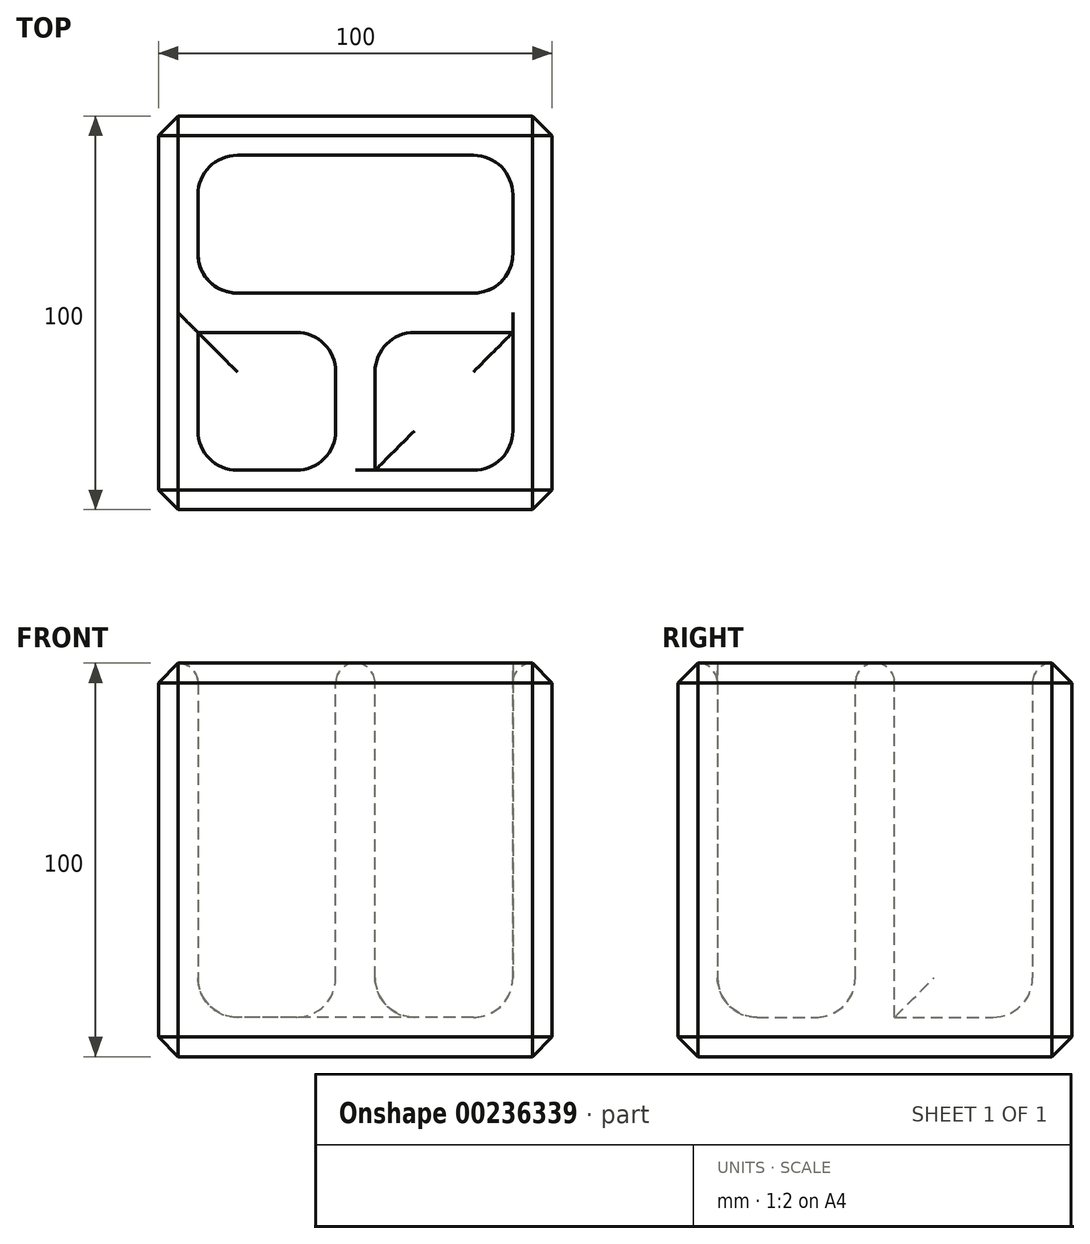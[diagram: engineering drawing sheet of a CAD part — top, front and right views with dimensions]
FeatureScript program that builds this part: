
annotation { "Feature Type Name" : "Feature", "Feature Type Description" : "" }
export const myFeature = defineFeature(function(context is Context, id is Id, definition is map)
    precondition{}
    {
        {
            var Q0;
            Q0=qCreatedBy(makeId("Top.planeOp"),FACE);
            var sketch = newSketch(context, id + "F0", { "sketchPlane" : qUnion([Q0])});
            skLineSegment(sketch, "E0.bottom", {"start": v(50, -50) * mm, "end": v(-50, -50) * mm});
            skLineSegment(sketch, "E0.top", {"start": v(50, 50) * mm, "end": v(-50, 50) * mm});
            skLineSegment(sketch, "E0.left", {"start": v(50, -50) * mm, "end": v(50, 50) * mm});
            skLineSegment(sketch, "E0.right", {"start": v(-50, -50) * mm, "end": v(-50, 50) * mm});
            skPoint(sketch, "E0.middle", {"position": v(0, 0) * mm});
            skSolve(sketch);
        }
        {
            var Q0;
            Q0 = qSketchRegion(id + "F0", true);
            extrude(context, id + "F1", {"entities" : qUnion([Q0]), "depth" : 100 * mm});
        }
        {
            var Q0;
            Q0=makeQuery(id+"F1.opExtrude","CAP_FACE",FACE,{"disambiguationData":[OSD([sQuery(id+"F0.wireOp",EDGE,"E0.bottom"),sQuery(id+"F0.wireOp",EDGE,"E0.top"),sQuery(id+"F0.wireOp",EDGE,"E0.left"),sQuery(id+"F0.wireOp",EDGE,"E0.right")])],"isStart":false});
            shell(context, id + "F2", {"entities" : qUnion([Q0]), "thickness" : 10 * mm});
        }
        {
            var Q0;
            Q0=makeQuery(id+"F1.opExtrude","CAP_FACE",FACE,{"disambiguationData":[OSD([sQuery(id+"F0.wireOp",EDGE,"E0.bottom"),sQuery(id+"F0.wireOp",EDGE,"E0.top"),sQuery(id+"F0.wireOp",EDGE,"E0.left"),sQuery(id+"F0.wireOp",EDGE,"E0.right")])],"isStart":false});
            var sketch = newSketch(context, id + "F3", { "sketchPlane" : qUnion([Q0])});
            skLineSegment(sketch, "E1", {"start": v(-40, -40) * mm, "end": v(-40, -5) * mm});
            skLineSegment(sketch, "E2", {"start": v(-40, 40) * mm, "end": v(-40, 5) * mm});
            skLineSegment(sketch, "E3", {"start": v(-40, -5) * mm, "end": v(-40, 5) * mm});
            skLineSegment(sketch, "E4", {"start": v(-40, -5) * mm, "end": v(40, -5) * mm});
            skLineSegment(sketch, "E5", {"start": v(-40, 5) * mm, "end": v(40, 5) * mm});
            skLineSegment(sketch, "E6", {"start": v(-40, 5) * mm, "end": v(-5, 5) * mm});
            skLineSegment(sketch, "E7", {"start": v(-5, 5) * mm, "end": v(5, 5) * mm});
            skLineSegment(sketch, "E8", {"start": v(-5, 5) * mm, "end": v(-5, 40) * mm});
            skLineSegment(sketch, "E9", {"start": v(-5, 5) * mm, "end": v(-5, -5) * mm});
            skLineSegment(sketch, "E10", {"start": v(-5, -5) * mm, "end": v(-5, -40) * mm});
            skLineSegment(sketch, "E11", {"start": v(5, 5) * mm, "end": v(5, 40) * mm});
            skLineSegment(sketch, "E12", {"start": v(5, 5) * mm, "end": v(5, -40) * mm});
            skSolve(sketch);
        }
        {
            var Q0;
            Q0 = qSketchRegion(id + "F3", true);
            var Q1;
            {var subQ0=sQuery(id+"F3.wireOp",EDGE,"E10");Q1=makeQuery(id+"F3.imprint","IMPRINT",FACE,{"disambiguationData":[TD([[makeQuery(id+"F3.imprint","IMPRINT",EDGE,{"derivedFrom":subQ0}),1.0]])]});}
            var Q2;
            Q2=makeQuery(id+"F3.imprint","IMPRINT",FACE,{"disambiguationData":[TD([[makeQuery(id+"F3.imprint","IMPRINT",EDGE,{"derivedFrom":sQuery(id+"F3.wireOp",EDGE,"E7")}),1.0]])]});
            var Q3;
            {var subQ6=sQuery(id+"F3.wireOp",EDGE,"E5");Q3=makeQuery(id+"F3.imprint","IMPRINT",FACE,{"disambiguationData":[TD([[makeQuery(id+"F3.imprint","IMPRINT",EDGE,{"derivedFrom":subQ6}),-1.0]])]});}
            extrude(context, id + "F4", {"entities" : qUnion([Q0, Q1, Q2, Q3]), "operationType" : NewBodyOperationType.ADD, "endBound" : BoundingType.UP_TO_NEXT, "oppositeDirection" : true, "depth" : 25 * mm});
        }
        {
            var Q0;
            Q0=makeQuery(id+"F1.opExtrude","CAP_EDGE",EDGE,{"disambiguationData":[OSD([sQuery(id+"F0.wireOp",EDGE,"E0.left")])],"isStart":false});
            var Q1;
            Q1=makeQuery(id+"F1.opExtrude","CAP_EDGE",EDGE,{"disambiguationData":[OSD([sQuery(id+"F0.wireOp",EDGE,"E0.bottom")])],"isStart":false});
            var Q2;
            Q2=makeQuery(id+"F1.opExtrude","CAP_EDGE",EDGE,{"disambiguationData":[OSD([sQuery(id+"F0.wireOp",EDGE,"E0.top")])],"isStart":false});
            var Q3;
            Q3=makeQuery(id+"F1.opExtrude","CAP_EDGE",EDGE,{"disambiguationData":[OSD([sQuery(id+"F0.wireOp",EDGE,"E0.right")])],"isStart":false});
            var Q4;
            Q4=makeQuery(id+"F1.opExtrude","SWEPT_EDGE",EDGE,{"disambiguationData":[OSD([sQuery(id+"F0.wireOp",EDGE,"E0.bottom"),sQuery(id+"F0.wireOp",EDGE,"E0.left")])]});
            var Q5;
            Q5=makeQuery(id+"F1.opExtrude","CAP_EDGE",EDGE,{"disambiguationData":[OSD([sQuery(id+"F0.wireOp",EDGE,"E0.left")])],"isStart":true});
            var Q6;
            Q6=makeQuery(id+"F1.opExtrude","CAP_EDGE",EDGE,{"disambiguationData":[OSD([sQuery(id+"F0.wireOp",EDGE,"E0.bottom")])],"isStart":true});
            var Q7;
            Q7=makeQuery(id+"F1.opExtrude","SWEPT_EDGE",EDGE,{"disambiguationData":[OSD([sQuery(id+"F0.wireOp",EDGE,"E0.bottom"),sQuery(id+"F0.wireOp",EDGE,"E0.right")])]});
            var Q8;
            Q8=makeQuery(id+"F1.opExtrude","CAP_EDGE",EDGE,{"disambiguationData":[OSD([sQuery(id+"F0.wireOp",EDGE,"E0.right")])],"isStart":true});
            var Q9;
            Q9=makeQuery(id+"F1.opExtrude","SWEPT_EDGE",EDGE,{"disambiguationData":[OSD([sQuery(id+"F0.wireOp",EDGE,"E0.top"),sQuery(id+"F0.wireOp",EDGE,"E0.right")])]});
            var Q10;
            Q10=makeQuery(id+"F1.opExtrude","CAP_EDGE",EDGE,{"disambiguationData":[OSD([sQuery(id+"F0.wireOp",EDGE,"E0.top")])],"isStart":true});
            var Q11;
            Q11=makeQuery(id+"F1.opExtrude","SWEPT_EDGE",EDGE,{"disambiguationData":[OSD([sQuery(id+"F0.wireOp",EDGE,"E0.top"),sQuery(id+"F0.wireOp",EDGE,"E0.left")])]});
            chamfer(context, id + "F5", {"entities" : qUnion([Q0, Q1, Q2, Q3, Q4, Q5, Q6, Q7, Q8, Q9, Q10, Q11]), "width" : 5 * mm, "tangentPropagation" : true});
        }
        {
            var Q0;
            Q0=makeQuery(id+"F2.opShell","OFFSET_EDGE",EDGE,{"disambiguationData":[OSD([sQuery(id+"F0.wireOp",EDGE,"E0.bottom"),sQuery(id+"F0.wireOp",EDGE,"E0.right")])]});
            var Q1;
            {var subQ0=sQuery(id+"F0.wireOp",EDGE,"E0.bottom");var subQ1=sQuery(id+"F0.wireOp",EDGE,"E0.right");Q1=makeQuery(id+"F4.boolean.opBoolean","SPLIT",EDGE,{"disambiguationData":[TD([makeQuery(id+"F2.opShell","OFFSET_FACE",FACE,{"disambiguationData":[OSD([subQ0])]})])],"derivedFrom":makeQuery(id+"F2.opShell","OFFSET_EDGE",EDGE,{"disambiguationData":[OSD([subQ1]),TDD([makeQuery(id+"F1.opExtrude","CAP_EDGE",EDGE,{"disambiguationData":[OSD([subQ1])],"isStart":true})])]})});}
            var Q2;
            Q2=makeQuery(id+"F4.opExtrude","SWEPT_EDGE",EDGE,{"disambiguationData":[OSD([sQuery(id+"F3.wireOp",EDGE,"E1"),sQuery(id+"F3.wireOp",EDGE,"E3"),sQuery(id+"F3.wireOp",EDGE,"E4")])]});
            var Q3;
            {var subQ0=sQuery(id+"F3.wireOp",EDGE,"E4");Q3=makeQuery(id+"F4.opExtrude","CAP_EDGE",EDGE,{"disambiguationData":[OSD([subQ0]),TDD([makeQuery(id+"F3.imprint","IMPRINT",EDGE,{"disambiguationData":[TD([[makeQuery(id+"F3.imprint","INTERSECT",VERTEX,{"derivedFrom":[sQuery(id+"F3.wireOp",EDGE,"E1"),sQuery(id+"F3.wireOp",EDGE,"E3"),subQ0]}),-1.0]])],"derivedFrom":subQ0})])],"isStart":false});}
            var Q4;
            Q4=makeQuery(id+"F4.opExtrude","CAP_EDGE",EDGE,{"disambiguationData":[OSD([sQuery(id+"F3.wireOp",EDGE,"E10")])],"isStart":false});
            var Q5;
            {var subQ0=sQuery(id+"F0.wireOp",EDGE,"E0.bottom");var subQ1=sQuery(id+"F0.wireOp",EDGE,"E0.right");Q5=makeQuery(id+"F4.boolean.opBoolean","SPLIT",EDGE,{"disambiguationData":[TD([makeQuery(id+"F2.opShell","OFFSET_FACE",FACE,{"disambiguationData":[OSD([subQ1])]})])],"derivedFrom":makeQuery(id+"F2.opShell","OFFSET_EDGE",EDGE,{"disambiguationData":[OSD([subQ0]),TDD([makeQuery(id+"F1.opExtrude","CAP_EDGE",EDGE,{"disambiguationData":[OSD([subQ0])],"isStart":true})])]})});}
            var Q6;
            Q6=makeQuery(id+"F4.opExtrude","SWEPT_EDGE",EDGE,{"disambiguationData":[OSD([sQuery(id+"F3.wireOp",EDGE,"E4"),sQuery(id+"F3.wireOp",EDGE,"E9"),sQuery(id+"F3.wireOp",EDGE,"E10")])]});
            var Q7;
            Q7=makeQuery(id+"F4.opExtrude","SWEPT_EDGE",EDGE,{"disambiguationData":[OSD([sQuery(id+"F0.wireOp",EDGE,"E0.bottom"),sQuery(id+"F3.wireOp",EDGE,"E10")])]});
            var Q8;
            Q8=makeQuery(id+"F4.opExtrude","SWEPT_EDGE",EDGE,{"disambiguationData":[OSD([sQuery(id+"F3.wireOp",EDGE,"E2"),sQuery(id+"F3.wireOp",EDGE,"E3"),sQuery(id+"F3.wireOp",EDGE,"E6")])]});
            var Q9;
            {var subQ0=sQuery(id+"F0.wireOp",EDGE,"E0.right");var subQ1=sQuery(id+"F0.wireOp",EDGE,"E0.top");Q9=makeQuery(id+"F4.boolean.opBoolean","SPLIT",EDGE,{"disambiguationData":[TD([makeQuery(id+"F2.opShell","OFFSET_FACE",FACE,{"disambiguationData":[OSD([subQ1])]})])],"derivedFrom":makeQuery(id+"F2.opShell","OFFSET_EDGE",EDGE,{"disambiguationData":[OSD([subQ0]),TDD([makeQuery(id+"F1.opExtrude","CAP_EDGE",EDGE,{"disambiguationData":[OSD([subQ0])],"isStart":true})])]})});}
            var Q10;
            Q10=makeQuery(id+"F4.opExtrude","CAP_EDGE",EDGE,{"disambiguationData":[OSD([sQuery(id+"F3.wireOp",EDGE,"E6")])],"isStart":false});
            var Q11;
            Q11=makeQuery(id+"F2.opShell","OFFSET_EDGE",EDGE,{"disambiguationData":[OSD([sQuery(id+"F0.wireOp",EDGE,"E0.top"),sQuery(id+"F0.wireOp",EDGE,"E0.right")])]});
            var Q12;
            {var subQ0=sQuery(id+"F0.wireOp",EDGE,"E0.right");var subQ1=sQuery(id+"F0.wireOp",EDGE,"E0.top");Q12=makeQuery(id+"F4.boolean.opBoolean","SPLIT",EDGE,{"disambiguationData":[TD([makeQuery(id+"F2.opShell","OFFSET_FACE",FACE,{"disambiguationData":[OSD([subQ0])]})])],"derivedFrom":makeQuery(id+"F2.opShell","OFFSET_EDGE",EDGE,{"disambiguationData":[OSD([subQ1]),TDD([makeQuery(id+"F1.opExtrude","CAP_EDGE",EDGE,{"disambiguationData":[OSD([subQ1])],"isStart":true})])]})});}
            var Q13;
            Q13=makeQuery(id+"F4.opExtrude","CAP_EDGE",EDGE,{"disambiguationData":[OSD([sQuery(id+"F3.wireOp",EDGE,"E8")])],"isStart":false});
            var Q14;
            Q14=makeQuery(id+"F4.opExtrude","SWEPT_EDGE",EDGE,{"disambiguationData":[OSD([sQuery(id+"F3.wireOp",EDGE,"E6"),sQuery(id+"F3.wireOp",EDGE,"E7"),sQuery(id+"F3.wireOp",EDGE,"E8"),sQuery(id+"F3.wireOp",EDGE,"E9")])]});
            var Q15;
            Q15=makeQuery(id+"F4.opExtrude","SWEPT_EDGE",EDGE,{"disambiguationData":[OSD([sQuery(id+"F0.wireOp",EDGE,"E0.top"),sQuery(id+"F3.wireOp",EDGE,"E8")])]});
            var Q16;
            Q16=makeQuery(id+"F4.opExtrude","CAP_EDGE",EDGE,{"disambiguationData":[OSD([sQuery(id+"F3.wireOp",EDGE,"E12")])],"isStart":false});
            var Q17;
            Q17=makeQuery(id+"F4.opExtrude","CAP_EDGE",EDGE,{"disambiguationData":[OSD([sQuery(id+"F3.wireOp",EDGE,"E11")])],"isStart":false});
            var Q18;
            {var subQ0=sQuery(id+"F0.wireOp",EDGE,"E0.left");var subQ1=sQuery(id+"F0.wireOp",EDGE,"E0.top");Q18=makeQuery(id+"F4.boolean.opBoolean","SPLIT",EDGE,{"disambiguationData":[TD([makeQuery(id+"F2.opShell","OFFSET_FACE",FACE,{"disambiguationData":[OSD([subQ0])]})])],"derivedFrom":makeQuery(id+"F2.opShell","OFFSET_EDGE",EDGE,{"disambiguationData":[OSD([subQ1]),TDD([makeQuery(id+"F1.opExtrude","CAP_EDGE",EDGE,{"disambiguationData":[OSD([subQ1])],"isStart":true})])]})});}
            var Q19;
            Q19=makeQuery(id+"F4.opExtrude","SWEPT_EDGE",EDGE,{"disambiguationData":[OSD([sQuery(id+"F0.wireOp",EDGE,"E0.top"),sQuery(id+"F3.wireOp",EDGE,"E11")])]});
            var Q20;
            Q20=makeQuery(id+"F4.opExtrude","SWEPT_EDGE",EDGE,{"disambiguationData":[OSD([sQuery(id+"F3.wireOp",EDGE,"E5"),sQuery(id+"F3.wireOp",EDGE,"E7"),sQuery(id+"F3.wireOp",EDGE,"E11"),sQuery(id+"F3.wireOp",EDGE,"E12")])]});
            var Q21;
            Q21=makeQuery(id+"F4.opExtrude","CAP_EDGE",EDGE,{"disambiguationData":[OSD([sQuery(id+"F3.wireOp",EDGE,"E5")])],"isStart":false});
            var Q22;
            Q22=makeQuery(id+"F2.opShell","OFFSET_EDGE",EDGE,{"disambiguationData":[OSD([sQuery(id+"F0.wireOp",EDGE,"E0.top"),sQuery(id+"F0.wireOp",EDGE,"E0.left")])]});
            var Q23;
            {var subQ0=sQuery(id+"F0.wireOp",EDGE,"E0.left");var subQ1=sQuery(id+"F0.wireOp",EDGE,"E0.top");Q23=makeQuery(id+"F4.boolean.opBoolean","SPLIT",EDGE,{"disambiguationData":[TD([makeQuery(id+"F2.opShell","OFFSET_FACE",FACE,{"disambiguationData":[OSD([subQ1])]})])],"derivedFrom":makeQuery(id+"F2.opShell","OFFSET_EDGE",EDGE,{"disambiguationData":[OSD([subQ0]),TDD([makeQuery(id+"F1.opExtrude","CAP_EDGE",EDGE,{"disambiguationData":[OSD([subQ0])],"isStart":true})])]})});}
            var Q24;
            Q24=makeQuery(id+"F4.opExtrude","SWEPT_EDGE",EDGE,{"disambiguationData":[OSD([sQuery(id+"F0.wireOp",EDGE,"E0.left"),sQuery(id+"F3.wireOp",EDGE,"E5")])]});
            var Q25;
            Q25=makeQuery(id+"F4.opExtrude","SWEPT_EDGE",EDGE,{"disambiguationData":[OSD([sQuery(id+"F3.wireOp",EDGE,"E4"),sQuery(id+"F3.wireOp",EDGE,"E12")])]});
            var Q26;
            {var subQ0=sQuery(id+"F3.wireOp",EDGE,"E4");Q26=makeQuery(id+"F4.opExtrude","CAP_EDGE",EDGE,{"disambiguationData":[OSD([subQ0]),TDD([makeQuery(id+"F3.imprint","IMPRINT",EDGE,{"disambiguationData":[TD([[makeQuery(id+"F3.imprint","INTERSECT",VERTEX,{"derivedFrom":[subQ0,sQuery(id+"F3.wireOp",EDGE,"E12")]}),-1.0]])],"derivedFrom":subQ0})])],"isStart":false});}
            var Q27;
            Q27=makeQuery(id+"F4.opExtrude","SWEPT_EDGE",EDGE,{"disambiguationData":[OSD([sQuery(id+"F0.wireOp",EDGE,"E0.bottom"),sQuery(id+"F3.wireOp",EDGE,"E12")])]});
            var Q28;
            {var subQ0=sQuery(id+"F0.wireOp",EDGE,"E0.bottom");var subQ1=sQuery(id+"F0.wireOp",EDGE,"E0.left");Q28=makeQuery(id+"F4.boolean.opBoolean","SPLIT",EDGE,{"disambiguationData":[TD([makeQuery(id+"F2.opShell","OFFSET_FACE",FACE,{"disambiguationData":[OSD([subQ1])]})])],"derivedFrom":makeQuery(id+"F2.opShell","OFFSET_EDGE",EDGE,{"disambiguationData":[OSD([subQ0]),TDD([makeQuery(id+"F1.opExtrude","CAP_EDGE",EDGE,{"disambiguationData":[OSD([subQ0])],"isStart":true})])]})});}
            var Q29;
            {var subQ0=sQuery(id+"F0.wireOp",EDGE,"E0.bottom");var subQ1=sQuery(id+"F0.wireOp",EDGE,"E0.left");Q29=makeQuery(id+"F4.boolean.opBoolean","SPLIT",EDGE,{"disambiguationData":[TD([makeQuery(id+"F2.opShell","OFFSET_FACE",FACE,{"disambiguationData":[OSD([subQ0])]})])],"derivedFrom":makeQuery(id+"F2.opShell","OFFSET_EDGE",EDGE,{"disambiguationData":[OSD([subQ1]),TDD([makeQuery(id+"F1.opExtrude","CAP_EDGE",EDGE,{"disambiguationData":[OSD([subQ1])],"isStart":true})])]})});}
            var Q30;
            Q30=makeQuery(id+"F4.opExtrude","SWEPT_EDGE",EDGE,{"disambiguationData":[OSD([sQuery(id+"F0.wireOp",EDGE,"E0.left"),sQuery(id+"F3.wireOp",EDGE,"E4")])]});
            var Q31;
            Q31=makeQuery(id+"F2.opShell","OFFSET_EDGE",EDGE,{"disambiguationData":[OSD([sQuery(id+"F0.wireOp",EDGE,"E0.bottom"),sQuery(id+"F0.wireOp",EDGE,"E0.left")])]});
            fillet(context, id + "F6", {"entities" : qUnion([Q0, Q1, Q2, Q3, Q4, Q5, Q6, Q7, Q8, Q9, Q10, Q11, Q12, Q13, Q14, Q15, Q16, Q17, Q18, Q19, Q20, Q21, Q22, Q23, Q24, Q25, Q26, Q27, Q28, Q29, Q30, Q31]), "radius" : 10 * mm, "tangentPropagation" : true, "allowEdgeOverflow" : false});
        }
        {
            var Q0;
            {var subQ5=sQuery(id+"F0.wireOp",EDGE,"E0.bottom");var subQ6=sQuery(id+"F0.wireOp",EDGE,"E0.right");Q0=makeQuery(id+"F4.boolean.opBoolean","SPLIT",EDGE,{"disambiguationData":[TD([makeQuery(id+"F2.opShell","OFFSET_FACE",FACE,{"disambiguationData":[OSD([subQ5])]})])],"derivedFrom":makeQuery(id+"F2.opShell","OFFSET_EDGE",EDGE,{"disambiguationData":[OSD([subQ6]),TDD([makeQuery(id+"F1.opExtrude","CAP_EDGE",EDGE,{"disambiguationData":[OSD([subQ6])],"isStart":false})])]})});}
            var Q1;
            {var subQ2=sQuery(id+"F0.wireOp",EDGE,"E0.top");var subQ4=sQuery(id+"F0.wireOp",EDGE,"E0.right");Q1=makeQuery(id+"F4.boolean.opBoolean","SPLIT",EDGE,{"disambiguationData":[TD([makeQuery(id+"F2.opShell","OFFSET_FACE",FACE,{"disambiguationData":[OSD([subQ2])]})])],"derivedFrom":makeQuery(id+"F2.opShell","OFFSET_EDGE",EDGE,{"disambiguationData":[OSD([subQ4]),TDD([makeQuery(id+"F1.opExtrude","CAP_EDGE",EDGE,{"disambiguationData":[OSD([subQ4])],"isStart":false})])]})});}
            var Q2;
            Q2=makeQuery(id+"F4.opExtrude","CAP_EDGE",EDGE,{"disambiguationData":[OSD([sQuery(id+"F3.wireOp",EDGE,"E11")])],"isStart":true});
            var Q3;
            Q3=makeQuery(id+"F4.opExtrude","CAP_EDGE",EDGE,{"disambiguationData":[OSD([sQuery(id+"F3.wireOp",EDGE,"E12")])],"isStart":true});
            fillet(context, id + "F7", {"entities" : qUnion([Q0, Q1, Q2, Q3]), "radius" : 5 * mm, "tangentPropagation" : true, "allowEdgeOverflow" : false});
        }
    });
